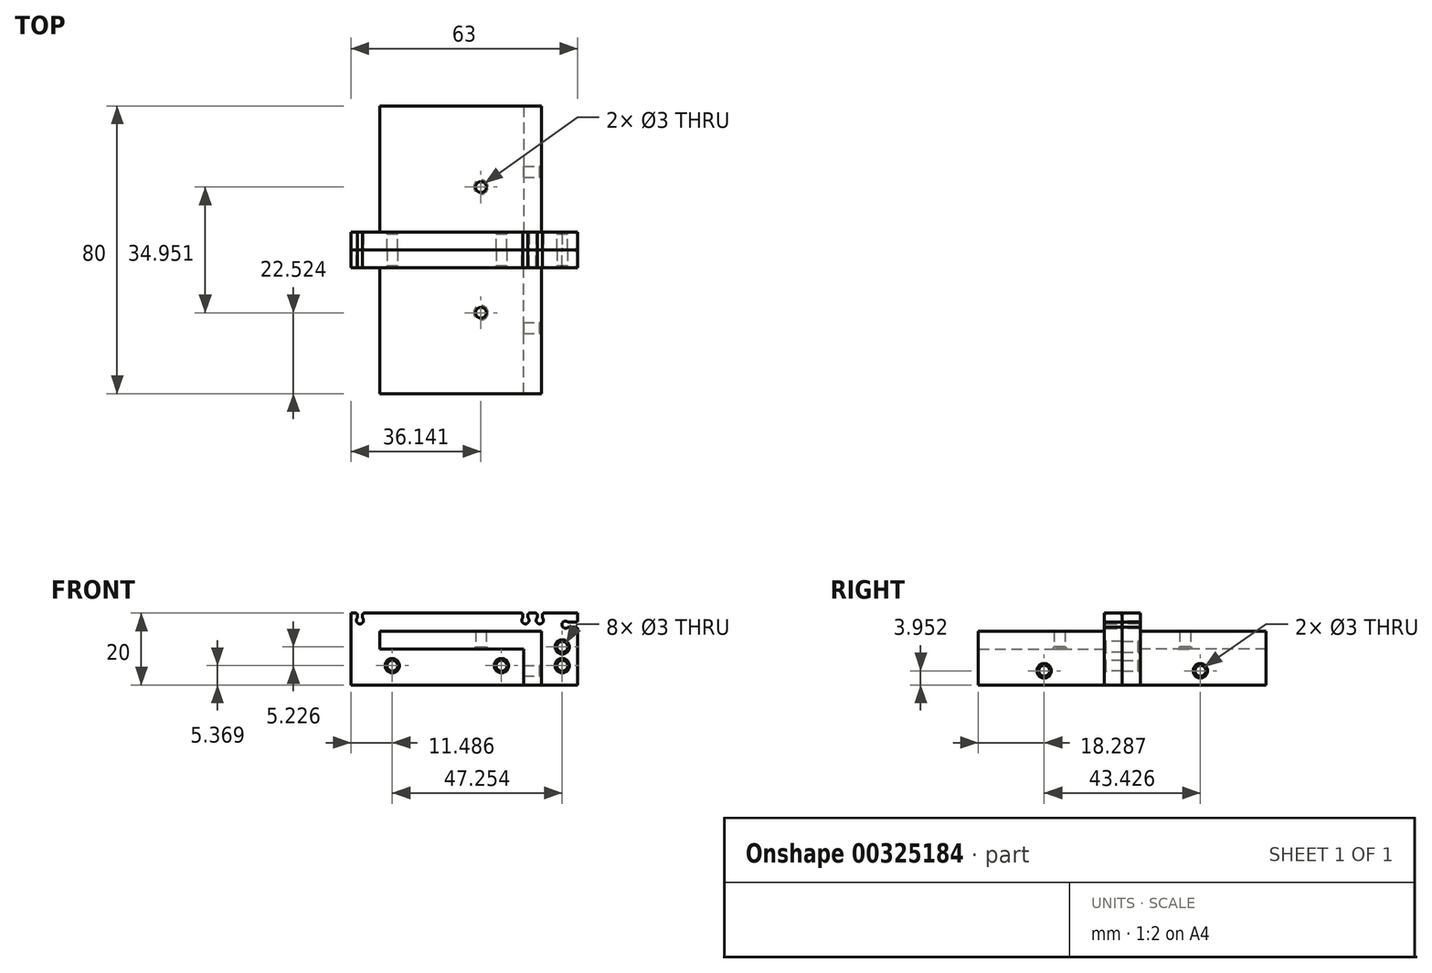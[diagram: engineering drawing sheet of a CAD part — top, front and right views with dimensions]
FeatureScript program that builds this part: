
annotation { "Feature Type Name" : "Feature", "Feature Type Description" : "" }
export const myFeature = defineFeature(function(context is Context, id is Id, definition is map)
    precondition{}
    {
        {
            var Q0;
            Q0=qCreatedBy(makeId("Front.planeOp"),FACE);
            var sketch = newSketch(context, id + "F0", { "sketchPlane" : qUnion([Q0])});
            skLineSegment(sketch, "E0.bottom", {"start": v(0, 0) * mm, "end": v(-55, 0) * mm});
            skLineSegment(sketch, "E0.top", {"start": v(0, 20) * mm, "end": v(-55, 20) * mm});
            skLineSegment(sketch, "E0.left", {"start": v(0, 0) * mm, "end": v(0, 20) * mm});
            skLineSegment(sketch, "E0.right", {"start": v(-55, 0) * mm, "end": v(-55, 20) * mm});
            skCircle(sketch, "E1", {"center": v(-52.5, 17.98) * mm, "radius": 1 * mm});
            skLineSegment(sketch, "E2", {"start": v(-52.5, 17.98) * mm, "end": v(-51.5, 17.98) * mm, "construction": true});
            skLineSegment(sketch, "E3", {"start": v(-52.5, 17.98) * mm, "end": v(-51.8, 18.69) * mm, "construction": true});
            skLineSegment(sketch, "E4", {"start": v(-51.8, 18.69) * mm, "end": v(-51.8, 20) * mm});
            skLineSegment(sketch, "E5", {"start": v(-53.2, 20) * mm, "end": v(-53.2, 18.69) * mm});
            skCircle(sketch, "E6", {"center": v(-2.5, 17.98) * mm, "radius": 1 * mm});
            skLineSegment(sketch, "E7", {"start": v(-2.5, 17.98) * mm, "end": v(-1.5, 17.98) * mm, "construction": true});
            skLineSegment(sketch, "E8", {"start": v(-2.5, 17.98) * mm, "end": v(-1.8, 18.69) * mm, "construction": true});
            skLineSegment(sketch, "E9", {"start": v(-1.8, 18.69) * mm, "end": v(-1.8, 20) * mm});
            skLineSegment(sketch, "E10", {"start": v(-3.2, 20) * mm, "end": v(-3.2, 18.69) * mm});
            skLineSegment(sketch, "E11.bottom", {"start": v(0, 0) * mm, "end": v(8, 0) * mm});
            skLineSegment(sketch, "E11.top", {"start": v(0, 20) * mm, "end": v(8, 20) * mm});
            skLineSegment(sketch, "E11.right", {"start": v(8, 0) * mm, "end": v(8, 20) * mm});
            skCircle(sketch, "E12", {"center": v(-6.5, 17.98) * mm, "radius": 1 * mm});
            skLineSegment(sketch, "E13", {"start": v(-6.5, 17.98) * mm, "end": v(-5.5, 17.98) * mm, "construction": true});
            skLineSegment(sketch, "E14", {"start": v(-6.5, 17.98) * mm, "end": v(-5.8, 18.69) * mm, "construction": true});
            skLineSegment(sketch, "E15", {"start": v(-5.8, 18.69) * mm, "end": v(-5.8, 20) * mm});
            skLineSegment(sketch, "E16", {"start": v(-7.2, 20) * mm, "end": v(-7.2, 18.69) * mm});
            skCircle(sketch, "E17", {"center": v(4.65, 16.76) * mm, "radius": 1 * mm});
            skLineSegment(sketch, "E18", {"start": v(4.65, 16.76) * mm, "end": v(4.65, 15.76) * mm, "construction": true});
            skLineSegment(sketch, "E19", {"start": v(4.65, 16.76) * mm, "end": v(5.35, 16.06) * mm, "construction": true});
            skLineSegment(sketch, "E20", {"start": v(5.35, 16.06) * mm, "end": v(8, 16.06) * mm});
            skLineSegment(sketch, "E21", {"start": v(8, 17.47) * mm, "end": v(5.35, 17.47) * mm});
            skSolve(sketch);
        }
        {
            var Q0;
            Q0=makeQuery(id+"F0.imprint","IMPRINT",FACE,{"disambiguationData":[TD([[makeQuery(id+"F0.imprint","IMPRINT",EDGE,{"derivedFrom":sQuery(id+"F0.wireOp",EDGE,"E0.bottom")}),-1.0]])]});
            var Q1;
            Q1=makeQuery(id+"F0.imprint","IMPRINT",FACE,{"disambiguationData":[TD([[makeQuery(id+"F0.imprint","IMPRINT",EDGE,{"derivedFrom":sQuery(id+"F0.wireOp",EDGE,"E11.bottom")}),1.0]])]});
            extrude(context, id + "F1", {"entities" : qUnion([Q0, Q1]), "depth" : 5 * mm});
        }
        {
            var Q0;
            Q0=makeQuery(id+"F1.opExtrude","SWEPT_FACE",FACE,{"disambiguationData":[OSD([sQuery(id+"F0.wireOp",EDGE,"E4")])]});
            var Q1;
            Q1=makeQuery(id+"F1.opExtrude","SWEPT_FACE",FACE,{"disambiguationData":[OSD([sQuery(id+"F0.wireOp",EDGE,"E1")])]});
            var Q2;
            Q2=makeQuery(id+"F1.opExtrude","SWEPT_FACE",FACE,{"disambiguationData":[OSD([sQuery(id+"F0.wireOp",EDGE,"E5")])]});
            var Q3;
            Q3=makeQuery(id+"F1.opExtrude","CAP_EDGE",EDGE,{"disambiguationData":[OSD([sQuery(id+"F0.wireOp",EDGE,"E1")])],"isStart":false});
            var Q4;
            Q4=makeQuery(id+"F1.opExtrude","SWEPT_EDGE",EDGE,{"disambiguationData":[OSD([sQuery(id+"F0.wireOp",EDGE,"E0.top"),sQuery(id+"F0.wireOp",EDGE,"E4")])]});
            var Q5;
            Q5=makeQuery(id+"F1.opExtrude","SWEPT_EDGE",EDGE,{"disambiguationData":[OSD([sQuery(id+"F0.wireOp",EDGE,"E0.top"),sQuery(id+"F0.wireOp",EDGE,"E5")])]});
            var Q6;
            Q6=makeQuery(id+"F1.opExtrude","SWEPT_EDGE",EDGE,{"disambiguationData":[OSD([sQuery(id+"F0.wireOp",EDGE,"E1"),sQuery(id+"F0.wireOp",EDGE,"E5")])]});
            var Q7;
            Q7=makeQuery(id+"F1.opExtrude","SWEPT_EDGE",EDGE,{"disambiguationData":[OSD([sQuery(id+"F0.wireOp",EDGE,"E1"),sQuery(id+"F0.wireOp",EDGE,"E4")])]});
            var Q8;
            Q8=makeQuery(id+"F1.opExtrude","CAP_EDGE",EDGE,{"disambiguationData":[OSD([sQuery(id+"F0.wireOp",EDGE,"E5")])],"isStart":false});
            var Q9;
            Q9=makeQuery(id+"F1.opExtrude","CAP_EDGE",EDGE,{"disambiguationData":[OSD([sQuery(id+"F0.wireOp",EDGE,"E1")])],"isStart":true});
            var Q10;
            Q10=makeQuery(id+"F1.opExtrude","CAP_EDGE",EDGE,{"disambiguationData":[OSD([sQuery(id+"F0.wireOp",EDGE,"E4")])],"isStart":false});
            var Q11;
            Q11=makeQuery(id+"F1.opExtrude","CAP_EDGE",EDGE,{"disambiguationData":[OSD([sQuery(id+"F0.wireOp",EDGE,"E4")])],"isStart":true});
            var Q12;
            Q12=makeQuery(id+"F1.opExtrude","CAP_EDGE",EDGE,{"disambiguationData":[OSD([sQuery(id+"F0.wireOp",EDGE,"E5")])],"isStart":true});
            var Q13;
            Q13=makeQuery(id+"F1.opExtrude","SWEPT_FACE",FACE,{"disambiguationData":[OSD([sQuery(id+"F0.wireOp",EDGE,"E9")])]});
            var Q14;
            Q14=makeQuery(id+"F1.opExtrude","SWEPT_FACE",FACE,{"disambiguationData":[OSD([sQuery(id+"F0.wireOp",EDGE,"E10")])]});
            var Q15;
            Q15=makeQuery(id+"F1.opExtrude","CAP_EDGE",EDGE,{"disambiguationData":[OSD([sQuery(id+"F0.wireOp",EDGE,"E6")])],"isStart":false});
            var Q16;
            Q16=makeQuery(id+"F1.opExtrude","SWEPT_FACE",FACE,{"disambiguationData":[OSD([sQuery(id+"F0.wireOp",EDGE,"E6")])]});
            var Q17;
            Q17=makeQuery(id+"F1.opExtrude","SWEPT_EDGE",EDGE,{"disambiguationData":[OSD([sQuery(id+"F0.wireOp",EDGE,"E6"),sQuery(id+"F0.wireOp",EDGE,"E9")])]});
            var Q18;
            Q18=makeQuery(id+"F1.opExtrude","SWEPT_EDGE",EDGE,{"disambiguationData":[OSD([sQuery(id+"F0.wireOp",EDGE,"E6"),sQuery(id+"F0.wireOp",EDGE,"E10")])]});
            var Q19;
            Q19=makeQuery(id+"F1.opExtrude","SWEPT_EDGE",EDGE,{"disambiguationData":[OSD([sQuery(id+"F0.wireOp",EDGE,"E0.top"),sQuery(id+"F0.wireOp",EDGE,"E9")])]});
            var Q20;
            Q20=makeQuery(id+"F1.opExtrude","SWEPT_EDGE",EDGE,{"disambiguationData":[OSD([sQuery(id+"F0.wireOp",EDGE,"E0.top"),sQuery(id+"F0.wireOp",EDGE,"E10")])]});
            var Q21;
            Q21=makeQuery(id+"F1.opExtrude","CAP_EDGE",EDGE,{"disambiguationData":[OSD([sQuery(id+"F0.wireOp",EDGE,"E6")])],"isStart":true});
            var Q22;
            Q22=makeQuery(id+"F1.opExtrude","CAP_EDGE",EDGE,{"disambiguationData":[OSD([sQuery(id+"F0.wireOp",EDGE,"E9")])],"isStart":false});
            var Q23;
            Q23=makeQuery(id+"F1.opExtrude","CAP_EDGE",EDGE,{"disambiguationData":[OSD([sQuery(id+"F0.wireOp",EDGE,"E10")])],"isStart":false});
            var Q24;
            Q24=makeQuery(id+"F1.opExtrude","CAP_EDGE",EDGE,{"disambiguationData":[OSD([sQuery(id+"F0.wireOp",EDGE,"E9")])],"isStart":true});
            var Q25;
            Q25=makeQuery(id+"F1.opExtrude","CAP_EDGE",EDGE,{"disambiguationData":[OSD([sQuery(id+"F0.wireOp",EDGE,"E10")])],"isStart":true});
            var Q26;
            Q26=makeQuery(id+"F1.opExtrude","CAP_EDGE",EDGE,{"disambiguationData":[OSD([sQuery(id+"F0.wireOp",EDGE,"E12")])],"isStart":false});
            var Q27;
            Q27=makeQuery(id+"F1.opExtrude","SWEPT_EDGE",EDGE,{"disambiguationData":[OSD([sQuery(id+"F0.wireOp",EDGE,"E12"),sQuery(id+"F0.wireOp",EDGE,"E15")])]});
            var Q28;
            Q28=makeQuery(id+"F1.opExtrude","CAP_EDGE",EDGE,{"disambiguationData":[OSD([sQuery(id+"F0.wireOp",EDGE,"E16")])],"isStart":false});
            var Q29;
            Q29=makeQuery(id+"F1.opExtrude","SWEPT_EDGE",EDGE,{"disambiguationData":[OSD([sQuery(id+"F0.wireOp",EDGE,"E12"),sQuery(id+"F0.wireOp",EDGE,"E16")])]});
            var Q30;
            Q30=makeQuery(id+"F1.opExtrude","CAP_EDGE",EDGE,{"disambiguationData":[OSD([sQuery(id+"F0.wireOp",EDGE,"E12")])],"isStart":true});
            var Q31;
            Q31=makeQuery(id+"F1.opExtrude","SWEPT_EDGE",EDGE,{"disambiguationData":[OSD([sQuery(id+"F0.wireOp",EDGE,"E0.top"),sQuery(id+"F0.wireOp",EDGE,"E15")])]});
            var Q32;
            Q32=makeQuery(id+"F1.opExtrude","CAP_EDGE",EDGE,{"disambiguationData":[OSD([sQuery(id+"F0.wireOp",EDGE,"E15")])],"isStart":false});
            var Q33;
            Q33=makeQuery(id+"F1.opExtrude","SWEPT_EDGE",EDGE,{"disambiguationData":[OSD([sQuery(id+"F0.wireOp",EDGE,"E0.top"),sQuery(id+"F0.wireOp",EDGE,"E16")])]});
            var Q34;
            Q34=makeQuery(id+"F1.opExtrude","CAP_EDGE",EDGE,{"disambiguationData":[OSD([sQuery(id+"F0.wireOp",EDGE,"E16")])],"isStart":true});
            var Q35;
            Q35=makeQuery(id+"F1.opExtrude","CAP_EDGE",EDGE,{"disambiguationData":[OSD([sQuery(id+"F0.wireOp",EDGE,"E15")])],"isStart":true});
            var Q36;
            Q36=makeQuery(id+"F1.opExtrude","CAP_EDGE",EDGE,{"disambiguationData":[OSD([sQuery(id+"F0.wireOp",EDGE,"E17")])],"isStart":false});
            var Q37;
            Q37=makeQuery(id+"F1.opExtrude","SWEPT_EDGE",EDGE,{"disambiguationData":[OSD([sQuery(id+"F0.wireOp",EDGE,"E17"),sQuery(id+"F0.wireOp",EDGE,"E21")])]});
            var Q38;
            Q38=makeQuery(id+"F1.opExtrude","SWEPT_EDGE",EDGE,{"disambiguationData":[OSD([sQuery(id+"F0.wireOp",EDGE,"E17"),sQuery(id+"F0.wireOp",EDGE,"E20")])]});
            var Q39;
            Q39=makeQuery(id+"F1.opExtrude","CAP_EDGE",EDGE,{"disambiguationData":[OSD([sQuery(id+"F0.wireOp",EDGE,"E20")])],"isStart":false});
            var Q40;
            Q40=makeQuery(id+"F1.opExtrude","CAP_EDGE",EDGE,{"disambiguationData":[OSD([sQuery(id+"F0.wireOp",EDGE,"E21")])],"isStart":false});
            var Q41;
            Q41=makeQuery(id+"F1.opExtrude","SWEPT_EDGE",EDGE,{"disambiguationData":[OSD([sQuery(id+"F0.wireOp",EDGE,"E11.right"),sQuery(id+"F0.wireOp",EDGE,"E20")])]});
            var Q42;
            Q42=makeQuery(id+"F1.opExtrude","CAP_EDGE",EDGE,{"disambiguationData":[OSD([sQuery(id+"F0.wireOp",EDGE,"E20")])],"isStart":true});
            var Q43;
            Q43=makeQuery(id+"F1.opExtrude","CAP_EDGE",EDGE,{"disambiguationData":[OSD([sQuery(id+"F0.wireOp",EDGE,"E21")])],"isStart":true});
            var Q44;
            Q44=makeQuery(id+"F1.opExtrude","SWEPT_EDGE",EDGE,{"disambiguationData":[OSD([sQuery(id+"F0.wireOp",EDGE,"E11.right"),sQuery(id+"F0.wireOp",EDGE,"E21")])]});
            var Q45;
            Q45=makeQuery(id+"F1.opExtrude","CAP_EDGE",EDGE,{"disambiguationData":[OSD([sQuery(id+"F0.wireOp",EDGE,"E17")])],"isStart":true});
            fillet(context, id + "F2", {"entities" : qUnion([Q0, Q1, Q2, Q3, Q4, Q5, Q6, Q7, Q8, Q9, Q10, Q11, Q12, Q13, Q14, Q15, Q16, Q17, Q18, Q19, Q20, Q21, Q22, Q23, Q24, Q25, Q26, Q27, Q28, Q29, Q30, Q31, Q32, Q33, Q34, Q35, Q36, Q37, Q38, Q39, Q40, Q41, Q42, Q43, Q44, Q45]), "radius" : 0.5 * mm, "tangentPropagation" : true, "allowEdgeOverflow" : false});
        }
        {
            var Q0;
            Q0=makeQuery(id+"F1.opExtrude","CAP_FACE",FACE,{"disambiguationData":[OSD([sQuery(id+"F0.wireOp",EDGE,"E0.bottom"),sQuery(id+"F0.wireOp",EDGE,"E0.top"),sQuery(id+"F0.wireOp",EDGE,"E0.right"),sQuery(id+"F0.wireOp",EDGE,"E1"),sQuery(id+"F0.wireOp",EDGE,"E4"),sQuery(id+"F0.wireOp",EDGE,"E5"),sQuery(id+"F0.wireOp",EDGE,"E6"),sQuery(id+"F0.wireOp",EDGE,"E9"),sQuery(id+"F0.wireOp",EDGE,"E10"),sQuery(id+"F0.wireOp",EDGE,"E11.bottom"),sQuery(id+"F0.wireOp",EDGE,"E11.top"),sQuery(id+"F0.wireOp",EDGE,"E11.right")])],"isStart":false});
            var sketch = newSketch(context, id + "F3", { "sketchPlane" : qUnion([Q0])});
            skLineSegment(sketch, "E22.bottom", {"start": v(-7, 15) * mm, "end": v(-2, 15) * mm});
            skLineSegment(sketch, "E22.top", {"start": v(-7, 0) * mm, "end": v(-2, 0) * mm});
            skLineSegment(sketch, "E22.left", {"start": v(-7, 15) * mm, "end": v(-7, 0) * mm});
            skLineSegment(sketch, "E22.right", {"start": v(-2, 15) * mm, "end": v(-2, 0) * mm});
            skLineSegment(sketch, "E23.bottom", {"start": v(-7, 15) * mm, "end": v(-47, 15) * mm});
            skLineSegment(sketch, "E23.top", {"start": v(-7, 10) * mm, "end": v(-47, 10) * mm});
            skLineSegment(sketch, "E23.left", {"start": v(-7, 15) * mm, "end": v(-7, 10) * mm});
            skLineSegment(sketch, "E23.right", {"start": v(-47, 15) * mm, "end": v(-47, 10) * mm});
            skLineSegment(sketch, "E24", {"start": v(-43.51, 5.37) * mm, "end": v(-13.15, 5.37) * mm, "construction": true});
            skLineSegment(sketch, "E25", {"start": v(-13.15, 5.37) * mm, "end": v(3.74, 5.37) * mm, "construction": true});
            skLineSegment(sketch, "E26", {"start": v(3.74, 5.37) * mm, "end": v(3.74, 10.6) * mm, "construction": true});
            skSolve(sketch);
        }
        {
            var Q0;
            Q0 = qSketchRegion(id + "F3", true);
            extrude(context, id + "F4", {"entities" : qUnion([Q0]), "operationType" : NewBodyOperationType.ADD, "depth" : 35 * mm});
        }
        {
            var Q0;
            Q0=makeQuery(id+"F4.opExtrude","SWEPT_FACE",FACE,{"disambiguationData":[OSD([sQuery(id+"F3.wireOp",EDGE,"E23.top")])]});
            var sketch = newSketch(context, id + "F5", { "sketchPlane" : qUnion([Q0])});
            skPoint(sketch, "E27", {"position": v(-18.86, 17.48) * mm});
            skSolve(sketch);
        }
        {
            var Q0;
            Q0=makeQuery(id+"F4.opExtrude","SWEPT_FACE",FACE,{"disambiguationData":[OSD([sQuery(id+"F3.wireOp",EDGE,"E22.right")])]});
            var sketch = newSketch(context, id + "F6", { "sketchPlane" : qUnion([Q0])});
            skPoint(sketch, "E28", {"position": v(-21.71, 3.95) * mm});
            skSolve(sketch);
        }
        {
            var Q0;
            Q0=sQuery(id+"F5.wireOp",VERTEX,"E27");
            var Q1;
            Q1=sQuery(id+"F6.wireOp",VERTEX,"E28");
            var Q2;
            Q2=sQuery(id+"F3.wireOp",VERTEX,"E24.start");
            var Q3;
            Q3=sQuery(id+"F3.wireOp",VERTEX,"E24.end");
            var Q4;
            Q4=sQuery(id+"F3.wireOp",VERTEX,"E25.end");
            var Q5;
            Q5=sQuery(id+"F3.wireOp",VERTEX,"E26.end");
            var Q6;
            Q6=makeQuery(id+"F1.opExtrude","SWEPT_BODY",BODY,{"disambiguationData":[OSD([sQuery(id+"F0.wireOp",EDGE,"E0.bottom"),sQuery(id+"F0.wireOp",EDGE,"E0.top"),sQuery(id+"F0.wireOp",EDGE,"E0.right"),sQuery(id+"F0.wireOp",EDGE,"E1"),sQuery(id+"F0.wireOp",EDGE,"E4"),sQuery(id+"F0.wireOp",EDGE,"E5"),sQuery(id+"F0.wireOp",EDGE,"E6"),sQuery(id+"F0.wireOp",EDGE,"E9"),sQuery(id+"F0.wireOp",EDGE,"E10"),sQuery(id+"F0.wireOp",EDGE,"E11.bottom"),sQuery(id+"F0.wireOp",EDGE,"E11.top"),sQuery(id+"F0.wireOp",EDGE,"E11.right")])]});
            hole(context, id + "F7", {"style" : HoleStyle.C_SINK, "endStyle" : HoleEndStyle.THROUGH, "holeDiameter" : 3 * mm, "cSinkDiameter" : 4 * mm, "cSinkAngle" : 82 * degree, "tappedDepth" : 12 * mm, "tapClearance" : 3, "locations" : qUnion([Q0, Q1, Q2, Q3, Q4, Q5]), "scope" : qUnion([Q6])});
        }
        {
            var Q0;
            Q0=makeQuery(id+"F1.opExtrude","SWEPT_BODY",BODY,{"disambiguationData":[OSD([sQuery(id+"F0.wireOp",EDGE,"E0.bottom"),sQuery(id+"F0.wireOp",EDGE,"E0.top"),sQuery(id+"F0.wireOp",EDGE,"E0.right"),sQuery(id+"F0.wireOp",EDGE,"E1"),sQuery(id+"F0.wireOp",EDGE,"E4"),sQuery(id+"F0.wireOp",EDGE,"E5"),sQuery(id+"F0.wireOp",EDGE,"E6"),sQuery(id+"F0.wireOp",EDGE,"E9"),sQuery(id+"F0.wireOp",EDGE,"E10"),sQuery(id+"F0.wireOp",EDGE,"E11.bottom"),sQuery(id+"F0.wireOp",EDGE,"E11.top"),sQuery(id+"F0.wireOp",EDGE,"E11.right")])]});
            var Q1;
            Q1=makeQuery(id+"F1.opExtrude","CAP_FACE",FACE,{"disambiguationData":[OSD([sQuery(id+"F0.wireOp",EDGE,"E0.bottom"),sQuery(id+"F0.wireOp",EDGE,"E0.top"),sQuery(id+"F0.wireOp",EDGE,"E0.right"),sQuery(id+"F0.wireOp",EDGE,"E1"),sQuery(id+"F0.wireOp",EDGE,"E4"),sQuery(id+"F0.wireOp",EDGE,"E5"),sQuery(id+"F0.wireOp",EDGE,"E6"),sQuery(id+"F0.wireOp",EDGE,"E9"),sQuery(id+"F0.wireOp",EDGE,"E10"),sQuery(id+"F0.wireOp",EDGE,"E11.bottom"),sQuery(id+"F0.wireOp",EDGE,"E11.top"),sQuery(id+"F0.wireOp",EDGE,"E11.right")])],"isStart":true});
            mirror(context, id + "F8", {"entities" : qUnion([Q0]), "mirrorPlane" : qUnion([Q1])});
        }
    });
